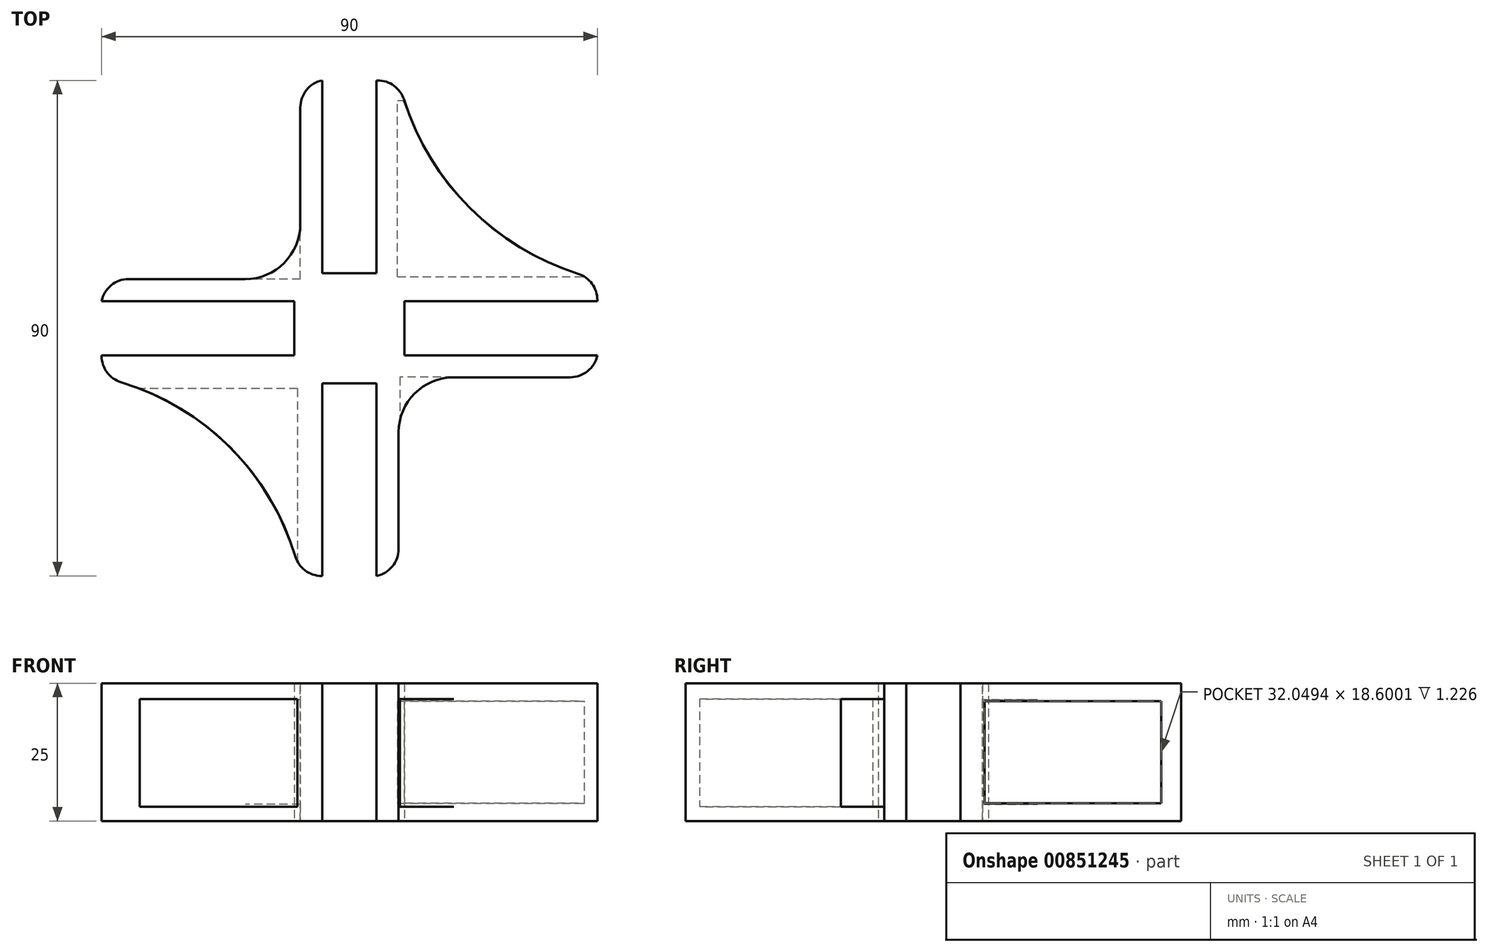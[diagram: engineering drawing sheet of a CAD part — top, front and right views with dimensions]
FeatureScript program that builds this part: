
annotation { "Feature Type Name" : "Feature", "Feature Type Description" : "" }
export const myFeature = defineFeature(function(context is Context, id is Id, definition is map)
    precondition{}
    {
        {
            var Q0;
            Q0=qCreatedBy(makeId("Top.planeOp"),FACE);
            var sketch = newSketch(context, id + "F0", { "sketchPlane" : qUnion([Q0])});
            skLineSegment(sketch, "E0.top", {"start": v(45, -45) * mm, "end": v(-45, -45) * mm, "construction": true});
            skLineSegment(sketch, "E0.left", {"start": v(45, 45) * mm, "end": v(45, -45) * mm, "construction": true});
            skLineSegment(sketch, "E1", {"start": v(0, 45) * mm, "end": v(0, -45) * mm, "construction": true});
            skLineSegment(sketch, "E2", {"start": v(-45, 0) * mm, "end": v(45, 0) * mm, "construction": true});
            skLineSegment(sketch, "E3", {"start": v(-4.92, 45) * mm, "end": v(-4.92, -45) * mm, "construction": true});
            skLineSegment(sketch, "E4", {"start": v(4.92, 45) * mm, "end": v(4.92, -45) * mm, "construction": true});
            skLineSegment(sketch, "E5", {"start": v(-45, 4.92) * mm, "end": v(45, 4.92) * mm, "construction": true});
            skLineSegment(sketch, "E6", {"start": v(-45, -4.92) * mm, "end": v(45, -4.92) * mm, "construction": true});
            skLineSegment(sketch, "E7", {"start": v(4.92, 45) * mm, "end": v(5.12, 45) * mm});
            skLineSegment(sketch, "E8", {"start": v(45, 4.92) * mm, "end": v(45, 5.12) * mm});
            skLineSegment(sketch, "E9", {"start": v(45, -4.92) * mm, "end": v(45, -8.92) * mm});
            skLineSegment(sketch, "E10", {"start": v(-45, -4.92) * mm, "end": v(-45, -5.06) * mm});
            skLineSegment(sketch, "E11", {"start": v(-4.92, 45) * mm, "end": v(-4.92, 10) * mm});
            skLineSegment(sketch, "E12", {"start": v(-4.92, 10) * mm, "end": v(4.92, 10) * mm});
            skLineSegment(sketch, "E13", {"start": v(4.92, 10) * mm, "end": v(4.92, 45) * mm});
            skLineSegment(sketch, "E14", {"start": v(-4.92, -45) * mm, "end": v(-4.92, -10) * mm});
            skLineSegment(sketch, "E15", {"start": v(-4.92, -10) * mm, "end": v(4.92, -10) * mm});
            skLineSegment(sketch, "E16", {"start": v(4.92, -10) * mm, "end": v(4.92, -45) * mm});
            skLineSegment(sketch, "E17", {"start": v(45, -4.92) * mm, "end": v(10, -4.92) * mm});
            skLineSegment(sketch, "E18", {"start": v(10, -4.92) * mm, "end": v(10, 4.92) * mm});
            skLineSegment(sketch, "E19", {"start": v(10, 4.92) * mm, "end": v(45, 4.92) * mm});
            skLineSegment(sketch, "E20", {"start": v(-45, 4.92) * mm, "end": v(-10, 4.92) * mm});
            skLineSegment(sketch, "E21", {"start": v(-10, 4.92) * mm, "end": v(-10, -4.92) * mm});
            skLineSegment(sketch, "E22", {"start": v(-10, -4.92) * mm, "end": v(-45, -4.92) * mm});
            skLineSegment(sketch, "E23", {"start": v(-4.92, -45) * mm, "end": v(-5.06, -45) * mm});
            skLineSegment(sketch, "E24", {"start": v(4.92, -45) * mm, "end": v(8.92, -45) * mm});
            skArc(sketch, "E25", {"start": v(9.88, 41.5) * mm, "mid": v(21.84, 21.84) * mm, "end": v(41.5, 9.88) * mm});
            skArc(sketch, "E26", {"start": v(-9.85, -41.44) * mm, "mid": v(-21.68, -21.68) * mm, "end": v(-41.45, -9.84) * mm});
            skPoint(sketch, "E27.visualSharp", {"position": v(-45, -8.92) * mm});
            skArc(sketch, "E27.filletArc", {"start": v(-45, -5.06) * mm, "mid": v(-44.01, -8.04) * mm, "end": v(-41.45, -9.84) * mm});
            skPoint(sketch, "E28.visualSharp", {"position": v(8.92, 45) * mm});
            skArc(sketch, "E28.filletArc", {"start": v(9.88, 41.5) * mm, "mid": v(8.07, 44.03) * mm, "end": v(5.12, 45) * mm});
            skLineSegment(sketch, "E29", {"start": v(8.92, -45) * mm, "end": v(8.92, -8.92) * mm});
            skLineSegment(sketch, "E30", {"start": v(8.92, -8.92) * mm, "end": v(45, -8.92) * mm});
            skLineSegment(sketch, "E31", {"start": v(-8.92, 8.92) * mm, "end": v(-45, 8.92) * mm});
            skLineSegment(sketch, "E32", {"start": v(-45, 8.92) * mm, "end": v(-45, 4.92) * mm});
            skLineSegment(sketch, "E33", {"start": v(-8.92, 8.92) * mm, "end": v(-8.92, 45) * mm});
            skLineSegment(sketch, "E34", {"start": v(-8.92, 45) * mm, "end": v(-4.92, 45) * mm});
            skLineSegment(sketch, "E35", {"start": v(41.5, 9.88) * mm, "end": v(45, 8.78) * mm});
            skLineSegment(sketch, "E36", {"start": v(45, 8.78) * mm, "end": v(45, 5.12) * mm});
            skLineSegment(sketch, "E37", {"start": v(-9.85, -41.44) * mm, "end": v(-8.77, -45) * mm});
            skLineSegment(sketch, "E38", {"start": v(-8.77, -45) * mm, "end": v(-4.92, -45) * mm});
            skSolve(sketch);
        }
        {
            var Q0;
            Q0=makeQuery(id+"F0.imprint","IMPRINT",FACE,{"disambiguationData":[TD([[makeQuery(id+"F0.imprint","IMPRINT",EDGE,{"derivedFrom":sQuery(id+"F0.wireOp",EDGE,"E7")}),-1.0]])]});
            extrude(context, id + "F1", {"entities" : qUnion([Q0]), "depth" : 25 * mm, "offsetDistance" : 25 * mm});
        }
        {
            var Q0;
            Q0=makeQuery(id+"F1.opExtrude","SWEPT_EDGE",EDGE,{"disambiguationData":[OSD([sQuery(id+"F0.wireOp",EDGE,"E29"),sQuery(id+"F0.wireOp",EDGE,"E30")])]});
            var Q1;
            Q1=makeQuery(id+"F1.opExtrude","SWEPT_EDGE",EDGE,{"disambiguationData":[OSD([sQuery(id+"F0.wireOp",EDGE,"E31"),sQuery(id+"F0.wireOp",EDGE,"E33")])]});
            fillet(context, id + "F2", {"entities" : qUnion([Q0, Q1]), "radius" : 10 * mm, "tangentPropagation" : true, "allowEdgeOverflow" : false});
        }
        {
            var Q0;
            Q0=makeQuery(id+"F1.opExtrude","SWEPT_FACE",FACE,{"disambiguationData":[OSD([sQuery(id+"F0.wireOp",EDGE,"E38")])]});
            var sketch = newSketch(context, id + "F3", { "sketchPlane" : qUnion([Q0])});
            skLineSegment(sketch, "E39.bottom", {"start": v(-9.44, 22.15) * mm, "end": v(-41.49, 22.15) * mm});
            skLineSegment(sketch, "E39.top", {"start": v(-9.44, 2.57) * mm, "end": v(-41.49, 2.57) * mm});
            skLineSegment(sketch, "E39.left", {"start": v(-9.44, 22.15) * mm, "end": v(-9.44, 2.57) * mm});
            skLineSegment(sketch, "E39.right", {"start": v(-41.49, 22.15) * mm, "end": v(-41.49, 2.57) * mm});
            skLineSegment(sketch, "E40.bottom", {"start": v(9.14, 22.15) * mm, "end": v(44.97, 22.15) * mm});
            skLineSegment(sketch, "E40.top", {"start": v(9.14, 2.57) * mm, "end": v(44.97, 2.57) * mm});
            skLineSegment(sketch, "E40.left", {"start": v(9.14, 22.15) * mm, "end": v(9.14, 2.57) * mm});
            skLineSegment(sketch, "E40.right", {"start": v(44.97, 22.15) * mm, "end": v(44.97, 2.57) * mm});
            skSolve(sketch);
        }
        {
            var Q0;
            Q0=makeQuery(id+"F3.imprint","IMPRINT",FACE,{"disambiguationData":[TD([[makeQuery(id+"F3.imprint","IMPRINT",EDGE,{"derivedFrom":sQuery(id+"F3.wireOp",EDGE,"E39.bottom")}),1.0]])]});
            extrude(context, id + "F4", {"entities" : qUnion([Q0]), "operationType" : NewBodyOperationType.REMOVE, "oppositeDirection" : true, "depth" : 34 * mm, "offsetDistance" : 25 * mm});
        }
        {
            var Q0;
            Q0=makeQuery(id+"F1.opExtrude","SWEPT_EDGE",EDGE,{"disambiguationData":[OSD([sQuery(id+"F0.wireOp",EDGE,"E37"),sQuery(id+"F0.wireOp",EDGE,"E38")])]});
            fillet(context, id + "F5", {"entities" : qUnion([Q0]), "radius" : 5 * mm, "tangentPropagation" : true, "allowEdgeOverflow" : false});
        }
        {
            var Q0;
            Q0=makeQuery(id+"F1.opExtrude","SWEPT_FACE",FACE,{"disambiguationData":[OSD([sQuery(id+"F0.wireOp",EDGE,"E8"),sQuery(id+"F0.wireOp",EDGE,"E36")])]});
            var sketch = newSketch(context, id + "F6", { "sketchPlane" : qUnion([Q0])});
            skLineSegment(sketch, "E41.bottom", {"start": v(9.32, 21.79) * mm, "end": v(41.37, 21.79) * mm});
            skLineSegment(sketch, "E41.top", {"start": v(9.32, 3.19) * mm, "end": v(41.37, 3.19) * mm});
            skLineSegment(sketch, "E41.left", {"start": v(9.32, 21.79) * mm, "end": v(9.32, 3.19) * mm});
            skLineSegment(sketch, "E41.right", {"start": v(41.37, 21.79) * mm, "end": v(41.37, 3.19) * mm});
            skSolve(sketch);
        }
        {
            var Q0;
            Q0=makeQuery(id+"F6.imprint","IMPRINT",FACE,{"disambiguationData":[TD([[makeQuery(id+"F6.imprint","IMPRINT",EDGE,{"derivedFrom":sQuery(id+"F6.wireOp",EDGE,"E41.bottom")}),-1.0]])]});
            extrude(context, id + "F7", {"entities" : qUnion([Q0]), "operationType" : NewBodyOperationType.REMOVE, "oppositeDirection" : true, "depth" : 36.3 * mm, "offsetDistance" : 25 * mm});
        }
        {
            var Q0;
            Q0=makeQuery(id+"F1.opExtrude","SWEPT_EDGE",EDGE,{"disambiguationData":[OSD([sQuery(id+"F0.wireOp",EDGE,"E35"),sQuery(id+"F0.wireOp",EDGE,"E36")])]});
            fillet(context, id + "F8", {"entities" : qUnion([Q0]), "radius" : 5 * mm, "tangentPropagation" : true, "allowEdgeOverflow" : false});
        }
        {
            var Q0;
            Q0=makeQuery(id+"F1.opExtrude","SWEPT_FACE",FACE,{"disambiguationData":[OSD([sQuery(id+"F0.wireOp",EDGE,"E34")])]});
            var sketch = newSketch(context, id + "F9", { "sketchPlane" : qUnion([Q0])});
            skLineSegment(sketch, "E42.bottom", {"start": v(8.92, 21.99) * mm, "end": v(45.06, 21.99) * mm});
            skLineSegment(sketch, "E42.top", {"start": v(8.92, 3) * mm, "end": v(45.06, 3) * mm});
            skLineSegment(sketch, "E42.left", {"start": v(8.92, 21.99) * mm, "end": v(8.92, 3) * mm});
            skLineSegment(sketch, "E42.right", {"start": v(45.06, 21.99) * mm, "end": v(45.06, 3) * mm});
            skSolve(sketch);
        }
        {
            var Q0;
            Q0 = qSketchRegion(id + "F9", true);
            extrude(context, id + "F10", {"entities" : qUnion([Q0]), "operationType" : NewBodyOperationType.REMOVE, "oppositeDirection" : true, "depth" : 36.1 * mm, "offsetDistance" : 25 * mm});
        }
        {
            var Q0;
            Q0=makeQuery(id+"F1.opExtrude","SWEPT_EDGE",EDGE,{"disambiguationData":[OSD([sQuery(id+"F0.wireOp",EDGE,"E33"),sQuery(id+"F0.wireOp",EDGE,"E34")])]});
            var Q1;
            {var subQ0=sQuery(id+"F0.wireOp",EDGE,"E31");var subQ1=sQuery(id+"F0.wireOp",EDGE,"E32");Q1=makeQuery(id+"F10.boolean.opBoolean","SPLIT",EDGE,{"disambiguationData":[TD([makeQuery(id+"F1.opExtrude","SWEPT_FACE",FACE,{"disambiguationData":[OSD([subQ0])]}),makeQuery(id+"F1.opExtrude","SWEPT_FACE",FACE,{"disambiguationData":[OSD([subQ1])]})])],"derivedFrom":makeQuery(id+"F1.opExtrude","SWEPT_EDGE",EDGE,{"disambiguationData":[OSD([subQ0,subQ1])]})});}
            fillet(context, id + "F11", {"entities" : qUnion([Q0, Q1]), "radius" : 5 * mm, "tangentPropagation" : true, "allowEdgeOverflow" : false});
        }
        {
            var Q0;
            Q0=makeQuery(id+"F3.imprint","IMPRINT",FACE,{"disambiguationData":[TD([[makeQuery(id+"F3.imprint","IMPRINT",EDGE,{"derivedFrom":sQuery(id+"F3.wireOp",EDGE,"E40.bottom")}),-1.0]])]});
            extrude(context, id + "F12", {"entities" : qUnion([Q0]), "operationType" : NewBodyOperationType.REMOVE, "oppositeDirection" : true, "depth" : 36.1 * mm, "offsetDistance" : 25 * mm});
        }
        {
            var Q0;
            Q0=makeQuery(id+"F1.opExtrude","SWEPT_EDGE",EDGE,{"disambiguationData":[OSD([sQuery(id+"F0.wireOp",EDGE,"E24"),sQuery(id+"F0.wireOp",EDGE,"E29")])]});
            fillet(context, id + "F13", {"entities" : qUnion([Q0]), "radius" : 5 * mm, "tangentPropagation" : true, "allowEdgeOverflow" : false});
        }
        {
            var Q0;
            Q0=makeQuery(id+"F1.opExtrude","SWEPT_EDGE",EDGE,{"disambiguationData":[OSD([sQuery(id+"F0.wireOp",EDGE,"E9"),sQuery(id+"F0.wireOp",EDGE,"E30")])]});
            fillet(context, id + "F14", {"entities" : qUnion([Q0]), "radius" : 5 * mm, "tangentPropagation" : true, "allowEdgeOverflow" : false});
        }
    });
